# Revit family: PRD_FrankeWS_WshbsnSpts_F5Aerator_ACXX1002
name_source: partatom
category: Specialty Equipment
revit_build: Autodesk Revit 2018 (Build: 20190510_1515(x64)
units: mm (PartAtom-declared; Revit-internal decimal feet)

## family parameters
Always vertical = No
Cut with Voids When Loaded = No
OmniClass Number = 23.45.05.14.99
OmniClass Title = Other Sanitary Washing Plumbing Fixtures
Part Type = Normal
Room Calculation Point = No
Round Connector Dimension = Use Diameter
Shared = No
Work Plane-Based = Yes

## types (1)
- ACXX1002
    AssetType = Fixed
    BIMObjectName = PRD_AR_WashbasinSpouts_F5Aerator_ACXX1002
    BodyMaterial = PRD_AR_ChromatedBrass_HighPolished
    Category = Pr_40_20_87_97, Washbasin spouts
    Default Elevation = 1219 mm
    Description = Theft-proof aerator, angle-adjustable +/- 6° in all directions, SLIM design, with integrated flow regulator 5.0 l/min, with male thread M 24 x 1, with mounting key.
    DurationUnit = year
    Features = integrated flow regulator 5.0 l/min
    GrossWeight = 0.04 kg
    IfcExportAs = IfcSanitaryTerminalType
    IfcExportType = USERDEFINED
    IntegralAccessories = with mounting key
    Manufacturer = KWC Group AG
    ManufacturerName = KWC Group AG
    ManufacturerURL = www.kwc.com
    Model = ACXX1002
    ModelNumber = 2030041326
    ModelReference = ACXX1002
    Name = F5 5.0 l/min. aerator, angle-adjustable ACXX1002
    NetWeight = 0.03 kg
    NominalDepth = 0 mm  [stored 0 ft]
    NominalHeight = 0 mm  [stored 0 ft]
    NominalLength = 0 mm  [stored 0 ft]
    NominalWidth = 0 mm  [stored 0 ft]
    ProductCode = 208.0578.963
    ProductInformation = https://pim.kwc.com
    Quantity = 1
    QuantityUom = Piece
    Status = New
    TailorMade = No
    URL = www.kwc.com
    Uniclass2015Code = Pr_40_20_87_97
    Uniclass2015Title = Washbasin spouts
    Uniclass2015Version = Products v1.23
    Version = 1
    WarrantyDurationUnit = year

note: [stored X ft] marks values corroborated as IEEE doubles in the binary element streams (Revit-internal decimal feet)

## geometry (parser evidence)
native form markers: Sweep x3
no freeform markers — native parametric forms only
